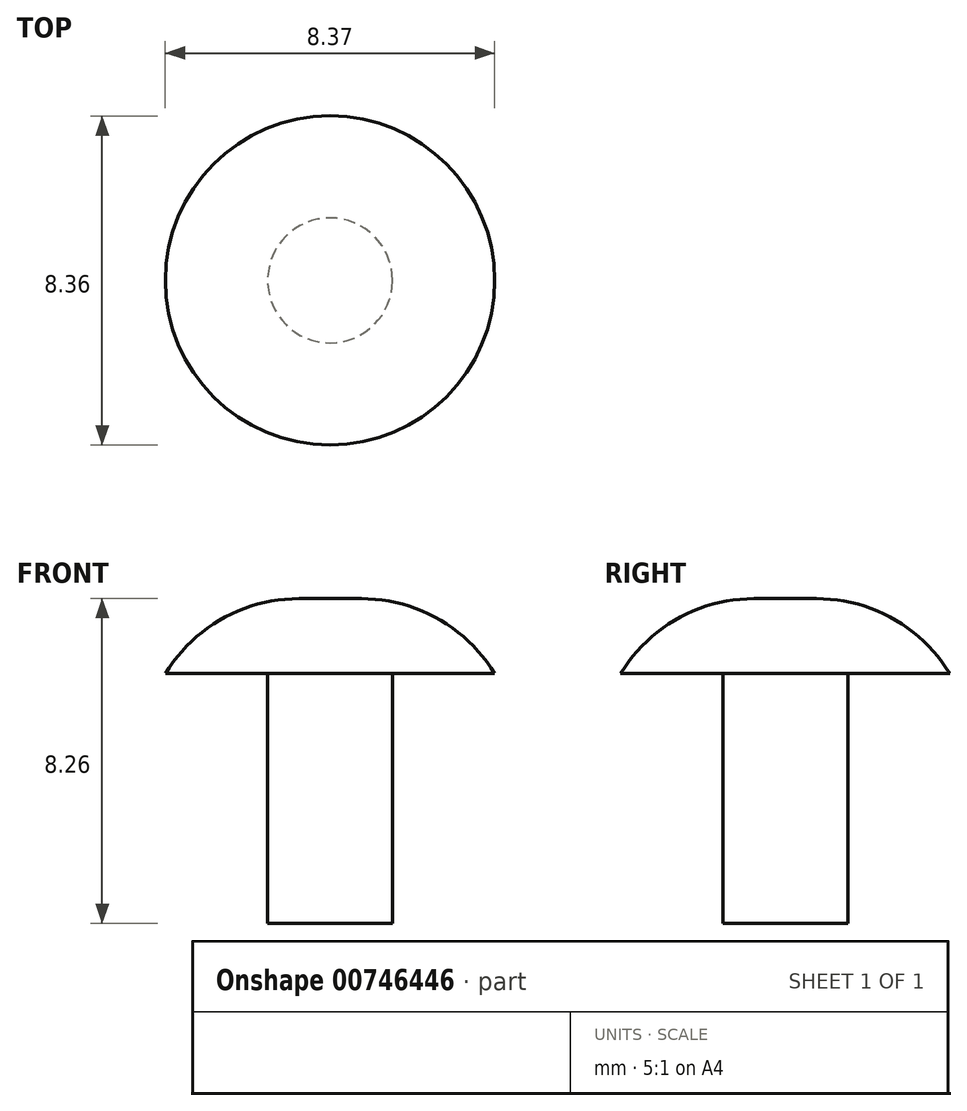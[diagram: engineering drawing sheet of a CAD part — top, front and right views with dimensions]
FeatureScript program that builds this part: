
annotation { "Feature Type Name" : "Feature", "Feature Type Description" : "" }
export const myFeature = defineFeature(function(context is Context, id is Id, definition is map)
    precondition{}
    {
        {
            var Q0;
            Q0=qCreatedBy(makeId("Front.planeOp"),FACE);
            var sketch = newSketch(context, id + "F0", { "sketchPlane" : qUnion([Q0])});
            skLineSegment(sketch, "E0", {"start": v(0, 0) * mm, "end": v(0.8, 0) * mm});
            skLineSegment(sketch, "E1", {"start": v(0, 0) * mm, "end": v(0, 8.26) * mm});
            skLineSegment(sketch, "E2", {"start": v(0, 8.26) * mm, "end": v(0, 4.29) * mm});
            skArc(sketch, "E3", {"start": v(0, 8.26) * mm, "mid": v(1.94, 7.75) * mm, "end": v(3.39, 6.35) * mm});
            skLineSegment(sketch, "E4", {"start": v(0.8, 0) * mm, "end": v(0.8, 6.35) * mm});
            skLineSegment(sketch, "E5", {"start": v(0.8, 6.35) * mm, "end": v(3.39, 6.35) * mm});
            skLineSegment(sketch, "E6", {"start": v(0.8, 0) * mm, "end": v(-0.8, 0) * mm});
            skLineSegment(sketch, "E7", {"start": v(-0.8, 0) * mm, "end": v(-0.8, 8.26) * mm});
            skLineSegment(sketch, "E8", {"start": v(-0.8, 8.26) * mm, "end": v(0, 8.26) * mm});
            skSolve(sketch);
        }
        {
            var Q0;
            {var subQ2=sQuery(id+"F0.wireOp",EDGE,"E1");Q0=makeQuery(id+"F0.imprint","IMPRINT",FACE,{"disambiguationData":[TD([[makeQuery(id+"F0.imprint","IMPRINT",EDGE,{"derivedFrom":subQ2}),1.0]])]});}
            var Q1;
            {var subQ1=sQuery(id+"F0.wireOp",EDGE,"E1");Q1=makeQuery(id+"F0.imprint","IMPRINT",FACE,{"disambiguationData":[TD([[makeQuery(id+"F0.imprint","IMPRINT",EDGE,{"derivedFrom":subQ1}),-1.0]])]});}
            var Q2;
            Q2=sQuery(id+"F0.wireOp",EDGE,"E7");
            revolve(context, id + "F1", {"entities" : qUnion([Q0, Q1]), "axis" : qUnion([Q2]), "revolveType" : RevolveType.FULL, "surfaceOperationType" : NewSurfaceOperationType.NEW});
        }
    });
